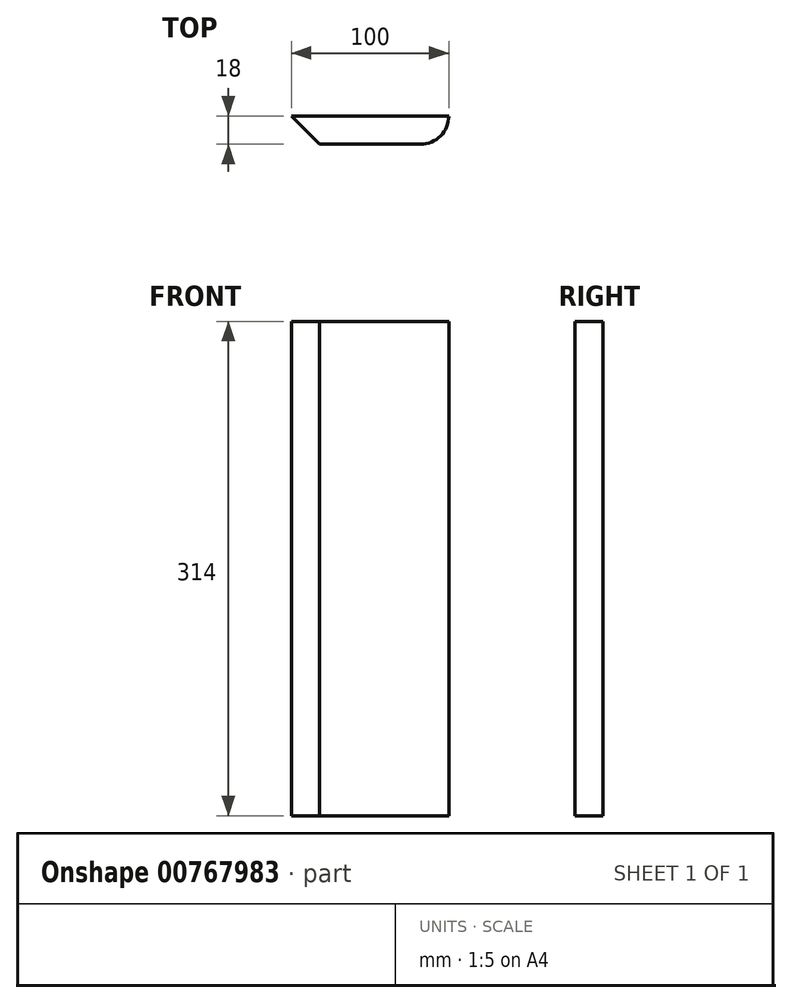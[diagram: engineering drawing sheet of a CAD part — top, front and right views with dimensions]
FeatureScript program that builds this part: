
annotation { "Feature Type Name" : "Feature", "Feature Type Description" : "" }
export const myFeature = defineFeature(function(context is Context, id is Id, definition is map)
    precondition{}
    {
        {
            var Q0;
            Q0=qCreatedBy(makeId("Front.planeOp"),FACE);
            var sketch = newSketch(context, id + "F0", { "sketchPlane" : qUnion([Q0])});
            skLineSegment(sketch, "E0.bottom", {"start": v(50, 157) * mm, "end": v(-50, 157) * mm});
            skLineSegment(sketch, "E0.top", {"start": v(50, -157) * mm, "end": v(-50, -157) * mm});
            skLineSegment(sketch, "E0.left", {"start": v(50, 157) * mm, "end": v(50, -157) * mm});
            skLineSegment(sketch, "E0.right", {"start": v(-50, 157) * mm, "end": v(-50, -157) * mm});
            skPoint(sketch, "E0.middle", {"position": v(0, 0) * mm});
            skSolve(sketch);
        }
        {
            var Q0;
            Q0 = qSketchRegion(id + "F0", true);
            extrude(context, id + "F1", {"entities" : qUnion([Q0]), "oppositeDirection" : true, "depth" : 18 * mm, "offsetDistance" : 25 * mm});
        }
        {
            var Q0;
            Q0=makeQuery(id+"F1.opExtrude","CAP_EDGE",EDGE,{"disambiguationData":[OSD([sQuery(id+"F0.wireOp",EDGE,"E0.right")])],"isStart":true});
            chamfer(context, id + "F2", {"entities" : qUnion([Q0]), "width" : 18 * mm, "tangentPropagation" : true});
        }
        {
            var Q0;
            Q0=makeQuery(id+"F1.opExtrude","CAP_EDGE",EDGE,{"disambiguationData":[OSD([sQuery(id+"F0.wireOp",EDGE,"E0.left")])],"isStart":true});
            fillet(context, id + "F3", {"entities" : qUnion([Q0]), "radius" : 18 * mm, "tangentPropagation" : true, "allowEdgeOverflow" : false});
        }
    });
